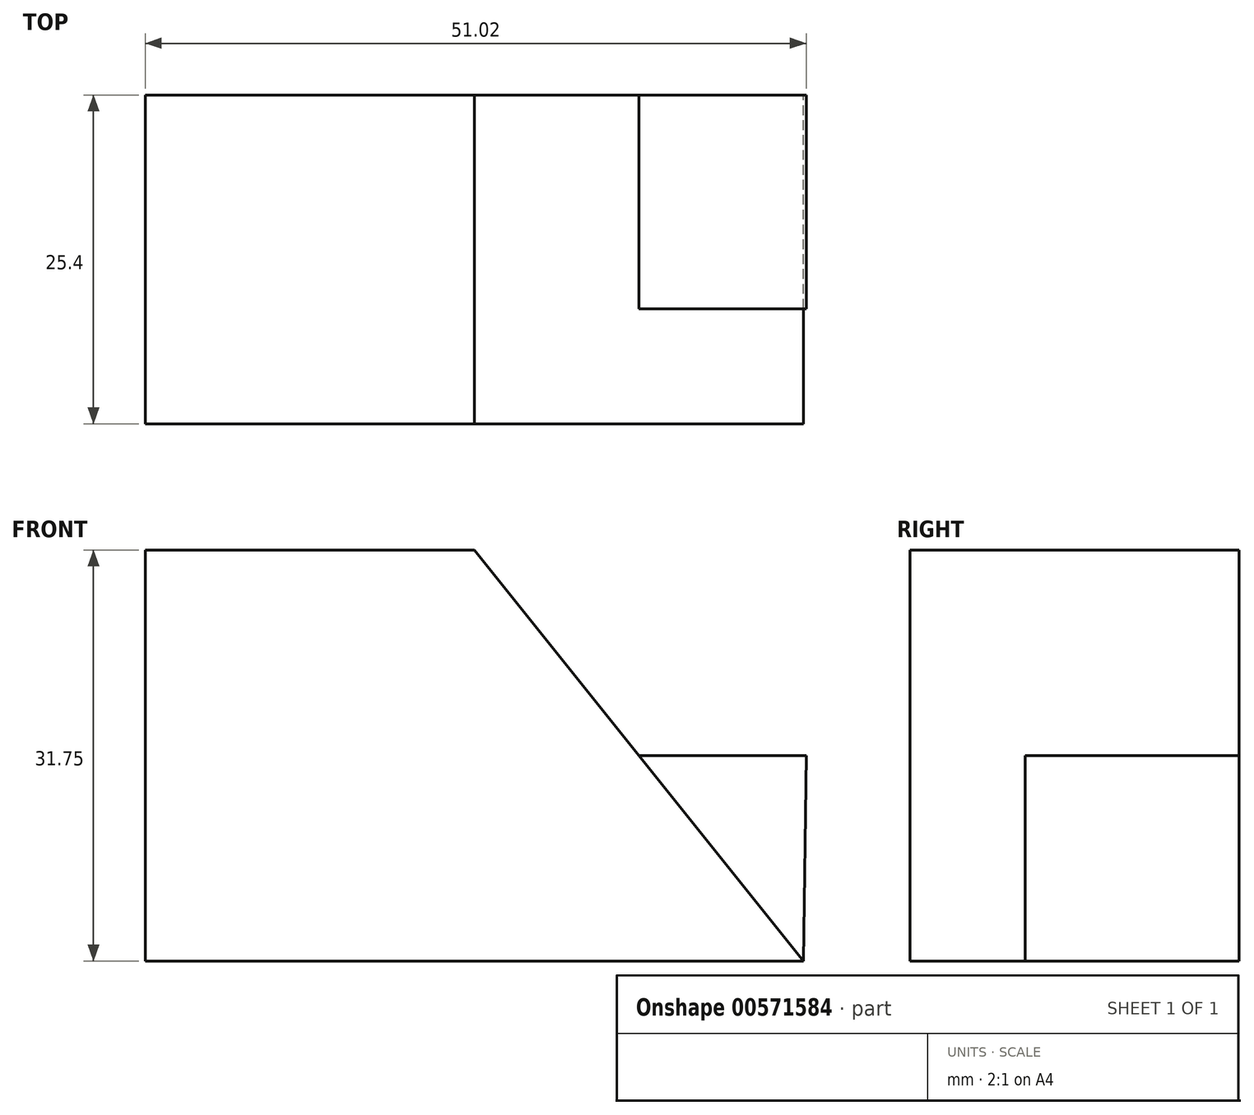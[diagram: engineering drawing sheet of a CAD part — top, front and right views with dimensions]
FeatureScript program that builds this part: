
annotation { "Feature Type Name" : "Feature", "Feature Type Description" : "" }
export const myFeature = defineFeature(function(context is Context, id is Id, definition is map)
    precondition{}
    {
        {
            var Q0;
            Q0=qCreatedBy(makeId("Front.planeOp"),FACE);
            var sketch = newSketch(context, id + "F0", { "sketchPlane" : qUnion([Q0])});
            skLineSegment(sketch, "E0", {"start": v(-55.13, 54.9) * mm, "end": v(-55.13, 23.14) * mm});
            skLineSegment(sketch, "E1", {"start": v(-55.13, 23.14) * mm, "end": v(-4.33, 23.14) * mm});
            skLineSegment(sketch, "E2", {"start": v(-4.33, 23.14) * mm, "end": v(-4.33, 54.9) * mm});
            skLineSegment(sketch, "E3", {"start": v(-4.33, 54.9) * mm, "end": v(-55.13, 54.9) * mm});
            skSolve(sketch);
        }
        {
            var Q0;
            Q0=makeQuery(id+"F0.imprint","IMPRINT",FACE,{"disambiguationData":[TD([[makeQuery(id+"F0.imprint","IMPRINT",EDGE,{"derivedFrom":sQuery(id+"F0.wireOp",EDGE,"E0")}),1.0]])]});
            extrude(context, id + "F1", {"entities" : qUnion([Q0]), "depth" : 25.4 * mm, "offsetDistance" : 25.4 * mm});
        }
        {
            var Q0;
            Q0=makeQuery(id+"F1.opExtrude","CAP_FACE",FACE,{"disambiguationData":[OSD([sQuery(id+"F0.wireOp",EDGE,"E0"),sQuery(id+"F0.wireOp",EDGE,"E1"),sQuery(id+"F0.wireOp",EDGE,"E2"),sQuery(id+"F0.wireOp",EDGE,"E3")])],"isStart":false});
            var sketch = newSketch(context, id + "F2", { "sketchPlane" : qUnion([Q0])});
            skLineSegment(sketch, "E4", {"start": v(-29.73, 54.9) * mm, "end": v(-4.33, 23.14) * mm});
            skSolve(sketch);
        }
        {
            var Q0;
            {var subQ0=sQuery(id+"F2.wireOp",EDGE,"E4");Q0=makeQuery(id+"F2.imprint","IMPRINT",FACE,{"disambiguationData":[TD([[makeQuery(id+"F2.imprint","IMPRINT",EDGE,{"derivedFrom":subQ0}),1.0]])]});}
            extrude(context, id + "F3", {"entities" : qUnion([Q0]), "operationType" : NewBodyOperationType.REMOVE, "endBound" : BoundingType.THROUGH_ALL, "oppositeDirection" : true, "depth" : 25.4 * mm, "offsetDistance" : 25.4 * mm});
        }
        {
            var Q0;
            Q0=makeQuery(id+"F1.opExtrude","CAP_FACE",FACE,{"disambiguationData":[OSD([sQuery(id+"F0.wireOp",EDGE,"E0"),sQuery(id+"F0.wireOp",EDGE,"E1"),sQuery(id+"F0.wireOp",EDGE,"E2"),sQuery(id+"F0.wireOp",EDGE,"E3")])],"isStart":true});
            var sketch = newSketch(context, id + "F4", { "sketchPlane" : qUnion([Q0])});
            skLineSegment(sketch, "E5", {"start": v(17.03, 39.02) * mm, "end": v(4.11, 39.02) * mm});
            skPoint(sketch, "E5.endSnap0", {"position": v(17.03, 39.02) * mm});
            skLineSegment(sketch, "E6", {"start": v(4.11, 39.02) * mm, "end": v(4.33, 23.14) * mm});
            skSolve(sketch);
        }
        {
            var Q0;
            {var subQ0=sQuery(id+"F4.wireOp",EDGE,"E5");Q0=makeQuery(id+"F4.imprint","IMPRINT",FACE,{"disambiguationData":[TD([[makeQuery(id+"F4.imprint","IMPRINT",EDGE,{"derivedFrom":subQ0}),1.0]])]});}
            extrude(context, id + "F5", {"entities" : qUnion([Q0]), "operationType" : NewBodyOperationType.ADD, "oppositeDirection" : true, "depth" : 16.5 * mm, "offsetDistance" : 25.4 * mm});
        }
    });
